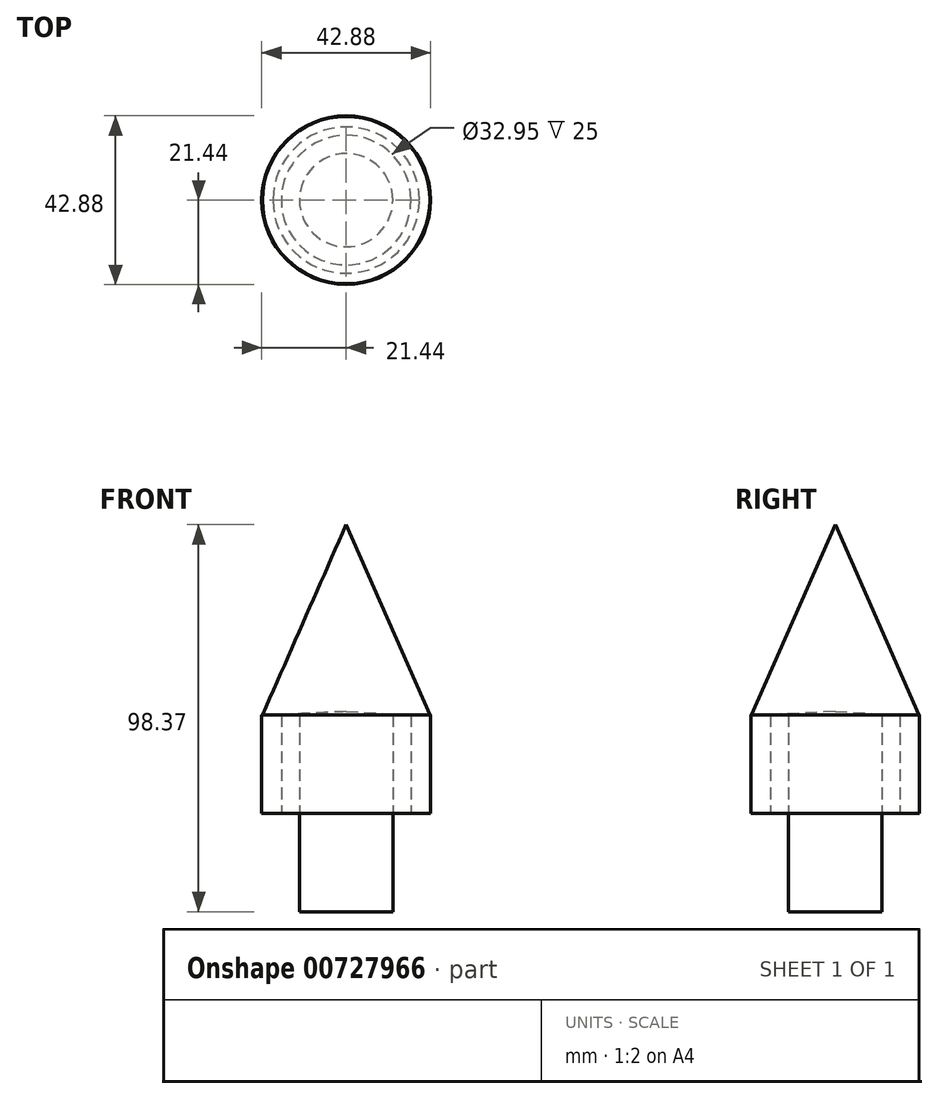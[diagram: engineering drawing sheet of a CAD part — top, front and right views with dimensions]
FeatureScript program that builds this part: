
annotation { "Feature Type Name" : "Feature", "Feature Type Description" : "" }
export const myFeature = defineFeature(function(context is Context, id is Id, definition is map)
    precondition{}
    {
        {
            var Q0;
            Q0=qCreatedBy(makeId("Top.planeOp"),FACE);
            var sketch = newSketch(context, id + "F0", { "sketchPlane" : qUnion([Q0])});
            skCircle(sketch, "E0", {"center": v(0, 0) * mm, "radius": 21.44 * mm});
            skCircle(sketch, "E1", {"center": v(0, 0) * mm, "radius": 19.35 * mm});
            skSolve(sketch);
        }
        {
            var Q0;
            Q0 = qSketchRegion(id + "F0", true);
            extrude(context, id + "F1", {"entities" : qUnion([Q0]), "depth" : 25 * mm, "offsetDistance" : 25 * mm});
        }
        {
            var Q0;
            Q0=qCreatedBy(makeId("Right.planeOp"),FACE);
            var sketch = newSketch(context, id + "F2", { "sketchPlane" : qUnion([Q0])});
            skLineSegment(sketch, "E2", {"start": v(-21.31, 24.87) * mm, "end": v(0, 73.37) * mm});
            skLineSegment(sketch, "E3", {"start": v(0, 73.37) * mm, "end": v(0, 25.87) * mm});
            skLineSegment(sketch, "E4", {"start": v(0, 25.87) * mm, "end": v(-21.31, 24.87) * mm});
            skLineSegment(sketch, "E5", {"start": v(0, 0) * mm, "end": v(0, 12.37) * mm});
            skSolve(sketch);
        }
        {
            var Q0;
            Q0 = qSketchRegion(id + "F2", true);
            var Q1;
            Q1=sQuery(id+"F2.wireOp",EDGE,"E5");
            revolve(context, id + "F3", {"operationType" : NewBodyOperationType.ADD, "surfaceOperationType" : NewSurfaceOperationType.NEW, "entities" : qUnion([Q0]), "axis" : qUnion([Q1]), "revolveType" : RevolveType.FULL});
        }
        {
            var Q0;
            Q0=qCreatedBy(makeId("Top.planeOp"),FACE);
            var sketch = newSketch(context, id + "F4", { "sketchPlane" : qUnion([Q0])});
            skCircle(sketch, "E6", {"center": v(0, 0) * mm, "radius": 19.35 * mm});
            skCircle(sketch, "E7", {"center": v(0, 0) * mm, "radius": 16.48 * mm});
            skSolve(sketch);
        }
        {
            var Q0;
            Q0 = qSketchRegion(id + "F4", true);
            extrude(context, id + "F5", {"entities" : qUnion([Q0]), "operationType" : NewBodyOperationType.ADD, "depth" : 25 * mm, "offsetDistance" : 25 * mm});
        }
        {
            var Q0;
            Q0=qCreatedBy(makeId("Top.planeOp"),FACE);
            var sketch = newSketch(context, id + "F6", { "sketchPlane" : qUnion([Q0])});
            skCircle(sketch, "E8", {"center": v(0, 0) * mm, "radius": 11.86 * mm});
            skSolve(sketch);
        }
        {
            var Q0;
            Q0=makeQuery(id+"F6.imprint","IMPRINT",FACE,{"disambiguationData":[TD([[makeQuery(id+"F6.imprint","IMPRINT",EDGE,{"derivedFrom":sQuery(id+"F6.wireOp",EDGE,"E8")}),1.0]])]});
            extrude(context, id + "F7", {"entities" : qUnion([Q0]), "depth" : 25 * mm, "offsetDistance" : 25 * mm});
        }
        {
            var Q0;
            Q0=makeQuery(id+"F7.opExtrude","CAP_FACE",FACE,{"disambiguationData":[OSD([sQuery(id+"F6.wireOp",EDGE,"E8")])],"isStart":true});
            extrude(context, id + "F8", {"entities" : qUnion([Q0]), "operationType" : NewBodyOperationType.ADD, "depth" : 25 * mm, "offsetDistance" : 25 * mm});
        }
    });
